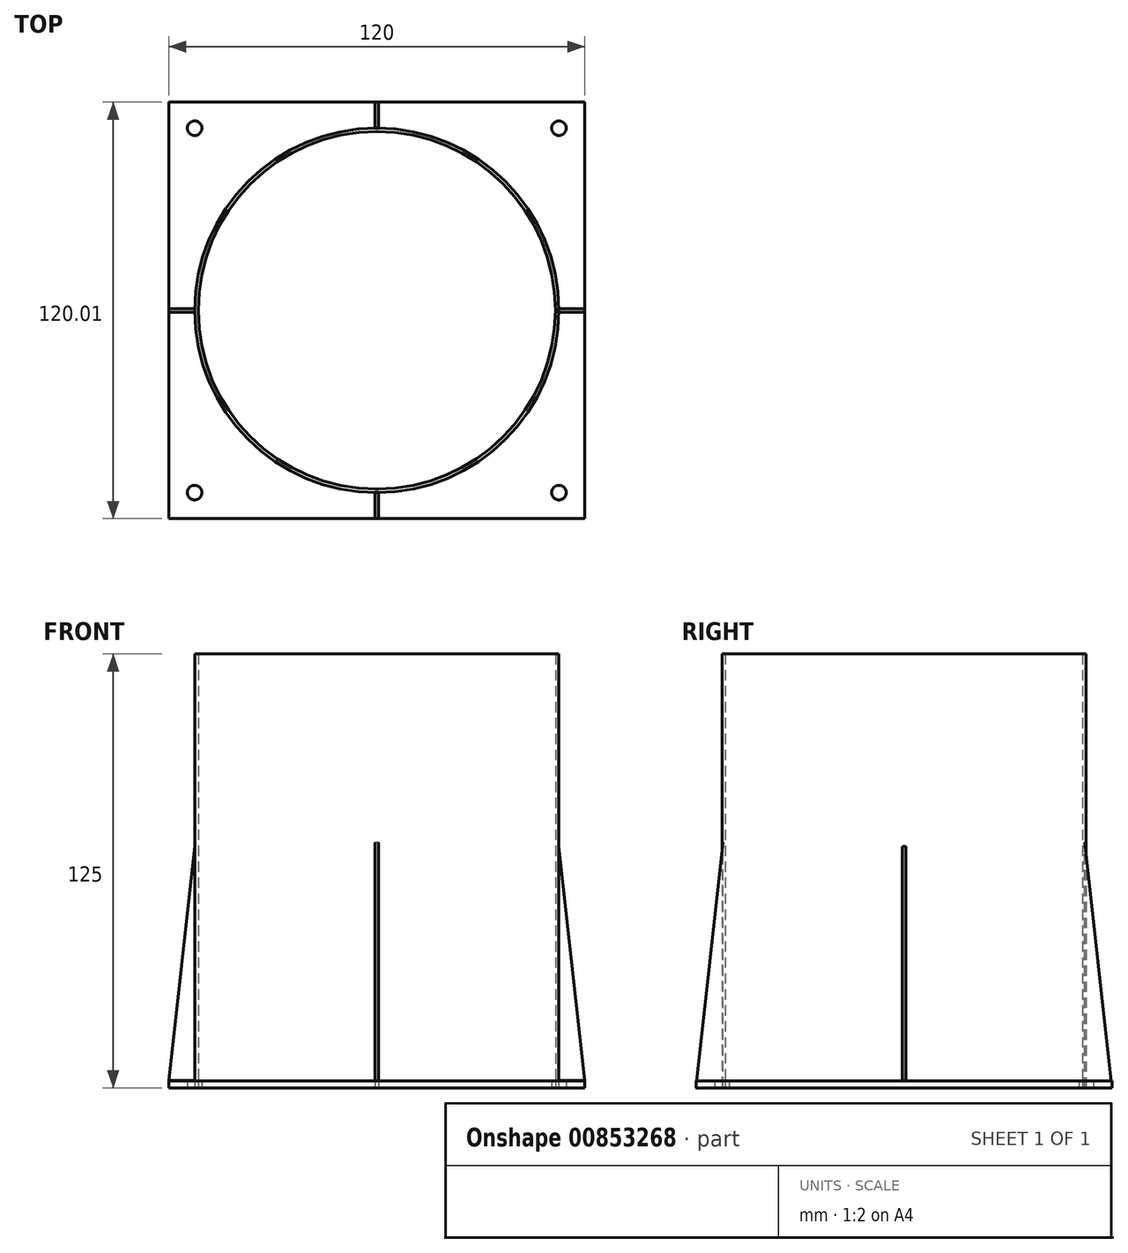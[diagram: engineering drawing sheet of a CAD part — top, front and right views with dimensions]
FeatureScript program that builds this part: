
annotation { "Feature Type Name" : "Feature", "Feature Type Description" : "" }
export const myFeature = defineFeature(function(context is Context, id is Id, definition is map)
    precondition{}
    {
        {
            var Q0;
            Q0=qCreatedBy(makeId("Top.planeOp"),FACE);
            var sketch = newSketch(context, id + "F0", { "sketchPlane" : qUnion([Q0])});
            skLineSegment(sketch, "E0.bottom", {"start": v(-60, 60) * mm, "end": v(60, 60) * mm});
            skLineSegment(sketch, "E0.top", {"start": v(-60, -60) * mm, "end": v(60, -60) * mm});
            skLineSegment(sketch, "E0.left", {"start": v(-60, 60) * mm, "end": v(-60, -60) * mm});
            skLineSegment(sketch, "E0.right", {"start": v(60, 60) * mm, "end": v(60, -60) * mm});
            skLineSegment(sketch, "E1.bottom", {"start": v(-52.5, 52.5) * mm, "end": v(52.5, 52.5) * mm});
            skLineSegment(sketch, "E1.top", {"start": v(-52.5, -52.5) * mm, "end": v(52.5, -52.5) * mm});
            skLineSegment(sketch, "E1.left", {"start": v(-52.5, 52.5) * mm, "end": v(-52.5, -52.5) * mm});
            skLineSegment(sketch, "E1.right", {"start": v(52.5, 52.5) * mm, "end": v(52.5, -52.5) * mm});
            skCircle(sketch, "E2", {"center": v(-52.5, 52.5) * mm, "radius": 2.1 * mm});
            skCircle(sketch, "E3", {"center": v(52.5, 52.5) * mm, "radius": 2.1 * mm});
            skCircle(sketch, "E4", {"center": v(52.5, -52.5) * mm, "radius": 2.1 * mm});
            skCircle(sketch, "E5", {"center": v(-52.5, -52.5) * mm, "radius": 2.1 * mm});
            skCircle(sketch, "E6", {"center": v(0, 0) * mm, "radius": 52.5 * mm});
            skPoint(sketch, "E6.first.point", {"position": v(0, 52.5) * mm});
            skPoint(sketch, "E6.second.point", {"position": v(0, -52.5) * mm});
            skPoint(sketch, "E6.third.point", {"position": v(-52.5, 0) * mm});
            skCircle(sketch, "E7", {"center": v(0, 0) * mm, "radius": 51.5 * mm});
            skSolve(sketch);
        }
        {
            var Q0;
            Q0=makeQuery(id+"F0.imprint","IMPRINT",FACE,{"disambiguationData":[TD([[makeQuery(id+"F0.imprint","IMPRINT",EDGE,{"derivedFrom":sQuery(id+"F0.wireOp",EDGE,"E0.bottom")}),-1.0]])]});
            var Q1;
            {var subQ0=sQuery(id+"F0.wireOp",EDGE,"E2");var subQ1=sQuery(id+"F0.wireOp",EDGE,"E1.bottom");var subQ2=makeQuery(id+"F0.imprint","INTERSECT",VERTEX,{"derivedFrom":[subQ1,subQ0]});Q1=makeQuery(id+"F0.imprint","IMPRINT",FACE,{"disambiguationData":[TD([[makeQuery(id+"F0.imprint","IMPRINT",EDGE,{"disambiguationData":[TD([[subQ2,-1.0]])],"derivedFrom":subQ1}),-1.0]])]});}
            var Q2;
            {var subQ0=sQuery(id+"F0.wireOp",EDGE,"E6");var subQ1=sQuery(id+"F0.wireOp",EDGE,"E1.bottom");var subQ2=makeQuery(id+"F0.imprint","INTERSECT",VERTEX,{"derivedFrom":[subQ1,subQ0]});Q2=makeQuery(id+"F0.imprint","IMPRINT",FACE,{"disambiguationData":[TD([[makeQuery(id+"F0.imprint","IMPRINT",EDGE,{"disambiguationData":[TD([[subQ2,-1.0]])],"derivedFrom":subQ1}),-1.0]])]});}
            var Q3;
            {var subQ0=sQuery(id+"F0.wireOp",EDGE,"E6");var subQ1=sQuery(id+"F0.wireOp",EDGE,"E1.top");var subQ2=makeQuery(id+"F0.imprint","INTERSECT",VERTEX,{"derivedFrom":[subQ1,subQ0]});Q3=makeQuery(id+"F0.imprint","IMPRINT",FACE,{"disambiguationData":[TD([[makeQuery(id+"F0.imprint","IMPRINT",EDGE,{"disambiguationData":[TD([[subQ2,-1.0]])],"derivedFrom":subQ1}),1.0]])]});}
            var Q4;
            {var subQ0=sQuery(id+"F0.wireOp",EDGE,"E5");var subQ1=sQuery(id+"F0.wireOp",EDGE,"E1.top");var subQ2=makeQuery(id+"F0.imprint","INTERSECT",VERTEX,{"derivedFrom":[subQ1,subQ0]});Q4=makeQuery(id+"F0.imprint","IMPRINT",FACE,{"disambiguationData":[TD([[makeQuery(id+"F0.imprint","IMPRINT",EDGE,{"disambiguationData":[TD([[subQ2,-1.0]])],"derivedFrom":subQ1}),1.0]])]});}
            var Q5;
            Q5=makeQuery(id+"F0.imprint","IMPRINT",FACE,{"disambiguationData":[TD([[makeQuery(id+"F0.imprint","IMPRINT",EDGE,{"derivedFrom":sQuery(id+"F0.wireOp",EDGE,"E7")}),-1.0]])]});
            extrude(context, id + "F1", {"entities" : qUnion([Q0, Q1, Q2, Q3, Q4, Q5]), "depth" : 2 * mm, "offsetDistance" : 25 * mm});
        }
        {
            var Q0;
            Q0=makeQuery(id+"F0.imprint","IMPRINT",FACE,{"disambiguationData":[TD([[makeQuery(id+"F0.imprint","IMPRINT",EDGE,{"derivedFrom":sQuery(id+"F0.wireOp",EDGE,"E7")}),-1.0]])]});
            extrude(context, id + "F2", {"entities" : qUnion([Q0]), "depth" : 125 * mm, "offsetDistance" : 25 * mm});
        }
        {
            var Q0;
            Q0=qCreatedBy(makeId("Front.planeOp"),FACE);
            var sketch = newSketch(context, id + "F3", { "sketchPlane" : qUnion([Q0])});
            skLineSegment(sketch, "E8", {"start": v(-60, 2.05) * mm, "end": v(-52.15, 2.05) * mm});
            skLineSegment(sketch, "E9", {"start": v(-52.15, 2.05) * mm, "end": v(-52.15, 72.77) * mm});
            skLineSegment(sketch, "E10", {"start": v(-52.15, 72.77) * mm, "end": v(-60, 2.05) * mm});
            skLineSegment(sketch, "E11.MirrorCS", {"start": v(60, 2.05) * mm, "end": v(52.15, 2.05) * mm});
            skLineSegment(sketch, "E12.MirrorCS", {"start": v(52.15, 72.77) * mm, "end": v(60, 2.05) * mm});
            skLineSegment(sketch, "E13.MirrorCS", {"start": v(52.15, 2.05) * mm, "end": v(52.15, 72.77) * mm});
            skSolve(sketch);
        }
        {
            var Q0;
            Q0=qCreatedBy(makeId("Right.planeOp"),FACE);
            var sketch = newSketch(context, id + "F4", { "sketchPlane" : qUnion([Q0])});
            skLineSegment(sketch, "E14", {"start": v(-60.01, 0) * mm, "end": v(-52.16, 0) * mm});
            skLineSegment(sketch, "E15", {"start": v(-52.16, 0) * mm, "end": v(-52.16, 70.72) * mm});
            skLineSegment(sketch, "E16", {"start": v(-52.16, 70.72) * mm, "end": v(-60.01, 0) * mm});
            skLineSegment(sketch, "E17.MirrorCS", {"start": v(59.98, 0) * mm, "end": v(52.13, 0) * mm});
            skLineSegment(sketch, "E18.MirrorCS", {"start": v(52.13, 70.72) * mm, "end": v(59.98, 0) * mm});
            skLineSegment(sketch, "E19.MirrorCS", {"start": v(52.13, 0) * mm, "end": v(52.13, 70.72) * mm});
            skSolve(sketch);
        }
        {
            var Q0;
            Q0 = qSketchRegion(id + "F3", true);
            extrude(context, id + "F5", {"entities" : qUnion([Q0]), "operationType" : NewBodyOperationType.ADD, "endBound" : BoundingType.SYMMETRIC, "depth" : 1 * mm, "offsetDistance" : 25 * mm});
        }
        {
            var Q0;
            Q0 = qSketchRegion(id + "F4", true);
            extrude(context, id + "F6", {"entities" : qUnion([Q0]), "endBound" : BoundingType.SYMMETRIC, "depth" : 1 * mm, "offsetDistance" : 25 * mm});
        }
    });
